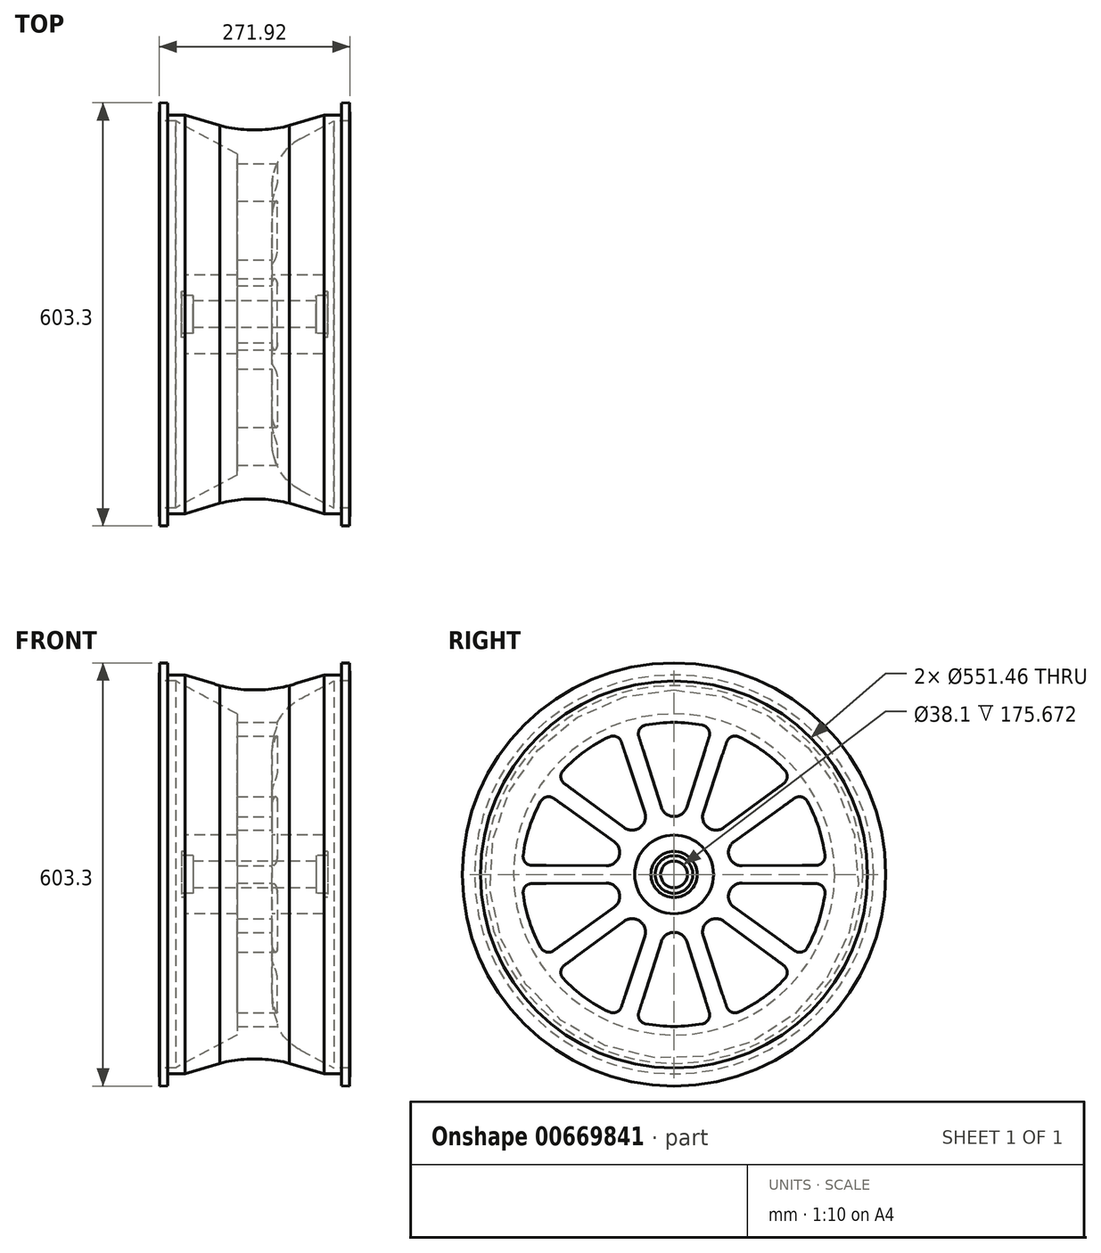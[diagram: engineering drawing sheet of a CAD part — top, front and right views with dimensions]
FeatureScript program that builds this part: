
annotation { "Feature Type Name" : "Feature", "Feature Type Description" : "" }
export const myFeature = defineFeature(function(context is Context, id is Id, definition is map)
    precondition{}
    {
        {
            var Q0;
            Q0=qCreatedBy(makeId("Front.planeOp"),FACE);
            var sketch = newSketch(context, id + "F0", { "sketchPlane" : qUnion([Q0])});
            skLineSegment(sketch, "E0", {"start": v(24.77, 228.87) * mm, "end": v(112.73, 275.73) * mm});
            skLineSegment(sketch, "E1", {"start": v(112.73, 275.73) * mm, "end": v(135.96, 275.73) * mm});
            skLineSegment(sketch, "E2", {"start": v(135.96, 275.73) * mm, "end": v(135.22, 301.65) * mm});
            skLineSegment(sketch, "E3", {"start": v(135.22, 301.65) * mm, "end": v(124.06, 301.33) * mm});
            skLineSegment(sketch, "E4", {"start": v(124.06, 301.33) * mm, "end": v(124.55, 284.39) * mm});
            skLineSegment(sketch, "E5", {"start": v(124.55, 284.39) * mm, "end": v(98.9, 284.39) * mm});
            skLineSegment(sketch, "E6", {"start": v(98.9, 284.39) * mm, "end": v(49.45, 269.2) * mm});
            skLineSegment(sketch, "E7", {"start": v(24.77, 228.87) * mm, "end": v(24.77, 56.11) * mm});
            skLineSegment(sketch, "E8", {"start": v(24.77, 56.11) * mm, "end": v(98.35, 56.11) * mm});
            skLineSegment(sketch, "E9", {"start": v(98.35, 56.11) * mm, "end": v(98.35, 32.88) * mm});
            skLineSegment(sketch, "E10", {"start": v(98.35, 32.88) * mm, "end": v(104.43, 32.88) * mm});
            skLineSegment(sketch, "E11", {"start": v(104.43, 32.88) * mm, "end": v(104.43, 26.8) * mm});
            skLineSegment(sketch, "E12", {"start": v(104.43, 26.8) * mm, "end": v(87.84, 26.8) * mm});
            skLineSegment(sketch, "E13", {"start": v(87.84, 26.8) * mm, "end": v(87.84, 19.05) * mm});
            skLineSegment(sketch, "E14", {"start": v(87.84, 19.05) * mm, "end": v(0, 19.05) * mm});
            skLineSegment(sketch, "E15.MirrorCS", {"start": v(-98.9, 284.39) * mm, "end": v(-49.45, 269.2) * mm});
            skLineSegment(sketch, "E16.MirrorCS", {"start": v(-124.55, 284.39) * mm, "end": v(-98.9, 284.39) * mm});
            skLineSegment(sketch, "E17.MirrorCS", {"start": v(-124.06, 301.33) * mm, "end": v(-124.55, 284.39) * mm});
            skLineSegment(sketch, "E18.MirrorCS", {"start": v(-104.43, 32.88) * mm, "end": v(-104.43, 26.8) * mm});
            skLineSegment(sketch, "E19.MirrorCS", {"start": v(-135.22, 301.65) * mm, "end": v(-124.06, 301.33) * mm});
            skLineSegment(sketch, "E20.MirrorCS", {"start": v(-98.35, 32.88) * mm, "end": v(-104.43, 32.88) * mm});
            skLineSegment(sketch, "E21.MirrorCS", {"start": v(-104.43, 26.8) * mm, "end": v(-87.84, 26.8) * mm});
            skLineSegment(sketch, "E22.MirrorCS", {"start": v(-87.84, 26.8) * mm, "end": v(-87.84, 19.05) * mm});
            skLineSegment(sketch, "E23.MirrorCS", {"start": v(-87.84, 19.05) * mm, "end": v(0, 19.05) * mm});
            skLineSegment(sketch, "E24.MirrorCS", {"start": v(-98.35, 56.11) * mm, "end": v(-98.35, 32.88) * mm});
            skLineSegment(sketch, "E25.MirrorCS", {"start": v(-112.73, 275.73) * mm, "end": v(-135.96, 275.73) * mm});
            skLineSegment(sketch, "E26.MirrorCS", {"start": v(-24.77, 228.87) * mm, "end": v(-112.73, 275.73) * mm});
            skLineSegment(sketch, "E27.MirrorCS", {"start": v(-135.96, 275.73) * mm, "end": v(-135.22, 301.65) * mm});
            skLineSegment(sketch, "E28.MirrorCS", {"start": v(-24.77, 56.11) * mm, "end": v(-98.35, 56.11) * mm});
            skLineSegment(sketch, "E29.MirrorCS", {"start": v(-24.77, 228.87) * mm, "end": v(-24.77, 56.11) * mm});
            skLineSegment(sketch, "E30", {"start": v(-56.5, 0) * mm, "end": v(51.37, 0) * mm});
            skArc(sketch, "E31", {"start": v(-49.45, 269.2) * mm, "mid": v(0, 262.95) * mm, "end": v(49.45, 269.2) * mm});
            skPoint(sketch, "E32.orphan", {"position": v(0, 254) * mm});
            skSolve(sketch);
        }
        {
            var Q0;
            Q0=makeQuery(id+"F0.imprint","IMPRINT",FACE,{"disambiguationData":[TD([[makeQuery(id+"F0.imprint","IMPRINT",EDGE,{"derivedFrom":sQuery(id+"F0.wireOp",EDGE,"E18.MirrorCS")}),1.0]])]});
            var Q1;
            Q1=sQuery(id+"F0.wireOp",EDGE,"E30");
            revolve(context, id + "F1", {"entities" : qUnion([Q0]), "axis" : qUnion([Q1]), "revolveType" : RevolveType.FULL});
        }
        {
            var Q0;
            Q0=makeQuery(id+"F1.opRevolve","SWEPT_FACE",FACE,{"disambiguationData":[OSD([sQuery(id+"F0.wireOp",EDGE,"E7")])]});
            var sketch = newSketch(context, id + "F2", { "sketchPlane" : qUnion([Q0])});
            skCircle(sketch, "E33", {"center": v(0, 0) * mm, "radius": 63.5 * mm});
            skCircle(sketch, "E34", {"center": v(0, 0) * mm, "radius": 69.85 * mm});
            skCircle(sketch, "E35", {"center": v(0, 0) * mm, "radius": 228.6 * mm});
            skCircle(sketch, "E36", {"center": v(0, 0) * mm, "radius": 222.25 * mm});
            skArc(sketch, "E37", {"start": v(50.2, 196.6) * mm, "mid": v(49, 206.95) * mm, "end": v(40.47, 212.92) * mm});
            skArc(sketch, "E38", {"start": v(-40.47, 212.92) * mm, "mid": v(-49, 206.95) * mm, "end": v(-50.2, 196.6) * mm});
            skArc(sketch, "E39", {"start": v(-18.15, 95.83) * mm, "mid": v(0, 82.55) * mm, "end": v(18.15, 95.83) * mm});
            skLineSegment(sketch, "E40", {"start": v(-50.2, 196.6) * mm, "end": v(-18.15, 95.83) * mm});
            skLineSegment(sketch, "E41", {"start": v(18.15, 95.83) * mm, "end": v(50.2, 196.6) * mm});
            skArc(sketch, "E42", {"start": v(40.47, 212.92) * mm, "mid": v(0, 216.73) * mm, "end": v(-40.47, 212.92) * mm});
            skArc(sketch, "E43.1.0", {"start": v(-74.94, 188.56) * mm, "mid": v(-82, 196.23) * mm, "end": v(-92.4, 196.04) * mm});
            skLineSegment(sketch, "E43.1.1", {"start": v(-156.17, 129.54) * mm, "end": v(-71.01, 66.85) * mm});
            skArc(sketch, "E43.1.2", {"start": v(-92.4, 196.04) * mm, "mid": v(-127.4, 175.34) * mm, "end": v(-157.9, 148.47) * mm});
            skLineSegment(sketch, "E43.1.3", {"start": v(-41.64, 88.2) * mm, "end": v(-74.94, 188.56) * mm});
            skArc(sketch, "E43.1.4", {"start": v(-71.01, 66.85) * mm, "mid": v(-48.52, 66.78) * mm, "end": v(-41.64, 88.2) * mm});
            skArc(sketch, "E43.1.5", {"start": v(-157.9, 148.47) * mm, "mid": v(-161.29, 138.62) * mm, "end": v(-156.17, 129.54) * mm});
            skArc(sketch, "E43.2.0", {"start": v(-171.46, 108.5) * mm, "mid": v(-181.67, 110.56) * mm, "end": v(-190, 104.29) * mm});
            skLineSegment(sketch, "E43.2.1", {"start": v(-202.49, 13) * mm, "end": v(-96.75, 12.35) * mm});
            skArc(sketch, "E43.2.2", {"start": v(-190, 104.29) * mm, "mid": v(-206.12, 66.97) * mm, "end": v(-215, 27.3) * mm});
            skLineSegment(sketch, "E43.2.3", {"start": v(-85.53, 46.88) * mm, "end": v(-171.46, 108.5) * mm});
            skArc(sketch, "E43.2.4", {"start": v(-96.75, 12.35) * mm, "mid": v(-78.5, 25.5) * mm, "end": v(-85.53, 46.88) * mm});
            skArc(sketch, "E43.2.5", {"start": v(-215, 27.3) * mm, "mid": v(-211.96, 17.34) * mm, "end": v(-202.49, 13) * mm});
            skArc(sketch, "E43.3.0", {"start": v(-202.49, -13) * mm, "mid": v(-211.96, -17.34) * mm, "end": v(-215, -27.3) * mm});
            skLineSegment(sketch, "E43.3.1", {"start": v(-171.46, -108.5) * mm, "end": v(-85.53, -46.88) * mm});
            skArc(sketch, "E43.3.2", {"start": v(-215, -27.3) * mm, "mid": v(-206.12, -66.97) * mm, "end": v(-190, -104.29) * mm});
            skLineSegment(sketch, "E43.3.3", {"start": v(-96.75, -12.35) * mm, "end": v(-202.49, -13) * mm});
            skArc(sketch, "E43.3.4", {"start": v(-85.53, -46.88) * mm, "mid": v(-78.5, -25.5) * mm, "end": v(-96.75, -12.35) * mm});
            skArc(sketch, "E43.3.5", {"start": v(-190, -104.29) * mm, "mid": v(-181.67, -110.56) * mm, "end": v(-171.46, -108.5) * mm});
            skArc(sketch, "E43.4.0", {"start": v(-156.17, -129.54) * mm, "mid": v(-161.29, -138.62) * mm, "end": v(-157.9, -148.47) * mm});
            skLineSegment(sketch, "E43.4.1", {"start": v(-74.94, -188.56) * mm, "end": v(-41.64, -88.2) * mm});
            skArc(sketch, "E43.4.2", {"start": v(-157.9, -148.47) * mm, "mid": v(-127.4, -175.34) * mm, "end": v(-92.4, -196.04) * mm});
            skLineSegment(sketch, "E43.4.3", {"start": v(-71.01, -66.85) * mm, "end": v(-156.17, -129.54) * mm});
            skArc(sketch, "E43.4.4", {"start": v(-41.64, -88.2) * mm, "mid": v(-48.52, -66.78) * mm, "end": v(-71.01, -66.85) * mm});
            skArc(sketch, "E43.4.5", {"start": v(-92.4, -196.04) * mm, "mid": v(-82, -196.23) * mm, "end": v(-74.94, -188.56) * mm});
            skArc(sketch, "E43.5.0", {"start": v(-50.2, -196.6) * mm, "mid": v(-49, -206.95) * mm, "end": v(-40.47, -212.92) * mm});
            skLineSegment(sketch, "E43.5.1", {"start": v(50.2, -196.6) * mm, "end": v(18.15, -95.83) * mm});
            skArc(sketch, "E43.5.2", {"start": v(-40.47, -212.92) * mm, "mid": v(0, -216.73) * mm, "end": v(40.47, -212.92) * mm});
            skLineSegment(sketch, "E43.5.3", {"start": v(-18.15, -95.83) * mm, "end": v(-50.2, -196.6) * mm});
            skArc(sketch, "E43.5.4", {"start": v(18.15, -95.83) * mm, "mid": v(0, -82.55) * mm, "end": v(-18.15, -95.83) * mm});
            skArc(sketch, "E43.5.5", {"start": v(40.47, -212.92) * mm, "mid": v(49, -206.95) * mm, "end": v(50.2, -196.6) * mm});
            skArc(sketch, "E43.6.0", {"start": v(74.94, -188.56) * mm, "mid": v(82, -196.23) * mm, "end": v(92.4, -196.04) * mm});
            skLineSegment(sketch, "E43.6.1", {"start": v(156.17, -129.54) * mm, "end": v(71.01, -66.85) * mm});
            skArc(sketch, "E43.6.2", {"start": v(92.4, -196.04) * mm, "mid": v(127.4, -175.34) * mm, "end": v(157.9, -148.47) * mm});
            skLineSegment(sketch, "E43.6.3", {"start": v(41.64, -88.2) * mm, "end": v(74.94, -188.56) * mm});
            skArc(sketch, "E43.6.4", {"start": v(71.01, -66.85) * mm, "mid": v(48.52, -66.78) * mm, "end": v(41.64, -88.2) * mm});
            skArc(sketch, "E43.6.5", {"start": v(157.9, -148.47) * mm, "mid": v(161.29, -138.62) * mm, "end": v(156.17, -129.54) * mm});
            skArc(sketch, "E43.7.0", {"start": v(171.46, -108.5) * mm, "mid": v(181.67, -110.56) * mm, "end": v(190, -104.29) * mm});
            skLineSegment(sketch, "E43.7.1", {"start": v(202.49, -13) * mm, "end": v(96.75, -12.35) * mm});
            skArc(sketch, "E43.7.2", {"start": v(190, -104.29) * mm, "mid": v(206.12, -66.97) * mm, "end": v(215, -27.3) * mm});
            skLineSegment(sketch, "E43.7.3", {"start": v(85.53, -46.88) * mm, "end": v(171.46, -108.5) * mm});
            skArc(sketch, "E43.7.4", {"start": v(96.75, -12.35) * mm, "mid": v(78.5, -25.5) * mm, "end": v(85.53, -46.88) * mm});
            skArc(sketch, "E43.7.5", {"start": v(215, -27.3) * mm, "mid": v(211.96, -17.34) * mm, "end": v(202.49, -13) * mm});
            skArc(sketch, "E43.8.0", {"start": v(202.49, 13) * mm, "mid": v(211.96, 17.34) * mm, "end": v(215, 27.3) * mm});
            skLineSegment(sketch, "E43.8.1", {"start": v(171.46, 108.5) * mm, "end": v(85.53, 46.88) * mm});
            skArc(sketch, "E43.8.2", {"start": v(215, 27.3) * mm, "mid": v(206.12, 66.97) * mm, "end": v(190, 104.29) * mm});
            skLineSegment(sketch, "E43.8.3", {"start": v(96.75, 12.35) * mm, "end": v(202.49, 13) * mm});
            skArc(sketch, "E43.8.4", {"start": v(85.53, 46.88) * mm, "mid": v(78.5, 25.5) * mm, "end": v(96.75, 12.35) * mm});
            skArc(sketch, "E43.8.5", {"start": v(190, 104.29) * mm, "mid": v(181.67, 110.56) * mm, "end": v(171.46, 108.5) * mm});
            skArc(sketch, "E43.9.0", {"start": v(156.17, 129.54) * mm, "mid": v(161.29, 138.62) * mm, "end": v(157.9, 148.47) * mm});
            skLineSegment(sketch, "E43.9.1", {"start": v(74.94, 188.56) * mm, "end": v(41.64, 88.2) * mm});
            skArc(sketch, "E43.9.2", {"start": v(157.9, 148.47) * mm, "mid": v(127.4, 175.34) * mm, "end": v(92.4, 196.04) * mm});
            skLineSegment(sketch, "E43.9.3", {"start": v(71.01, 66.85) * mm, "end": v(156.17, 129.54) * mm});
            skArc(sketch, "E43.9.4", {"start": v(41.64, 88.2) * mm, "mid": v(48.52, 66.78) * mm, "end": v(71.01, 66.85) * mm});
            skArc(sketch, "E43.9.5", {"start": v(92.4, 196.04) * mm, "mid": v(82, 196.23) * mm, "end": v(74.94, 188.56) * mm});
            skSolve(sketch);
        }
        {
            var Q0;
            {var subQ0=sQuery(id+"F2.wireOp",EDGE,"E43.2.4");Q0=makeQuery(id+"F2.imprint","IMPRINT",FACE,{"disambiguationData":[TD([[makeQuery(id+"F2.imprint","IMPRINT",EDGE,{"derivedFrom":subQ0}),1.0]])]});}
            var Q1;
            {var subQ0=sQuery(id+"F2.wireOp",EDGE,"E43.3.4");Q1=makeQuery(id+"F2.imprint","IMPRINT",FACE,{"disambiguationData":[TD([[makeQuery(id+"F2.imprint","IMPRINT",EDGE,{"derivedFrom":subQ0}),1.0]])]});}
            var Q2;
            {var subQ0=sQuery(id+"F2.wireOp",EDGE,"E43.4.4");Q2=makeQuery(id+"F2.imprint","IMPRINT",FACE,{"disambiguationData":[TD([[makeQuery(id+"F2.imprint","IMPRINT",EDGE,{"derivedFrom":subQ0}),1.0]])]});}
            var Q3;
            {var subQ0=sQuery(id+"F2.wireOp",EDGE,"E43.5.4");Q3=makeQuery(id+"F2.imprint","IMPRINT",FACE,{"disambiguationData":[TD([[makeQuery(id+"F2.imprint","IMPRINT",EDGE,{"derivedFrom":subQ0}),1.0]])]});}
            var Q4;
            {var subQ0=sQuery(id+"F2.wireOp",EDGE,"E43.6.4");Q4=makeQuery(id+"F2.imprint","IMPRINT",FACE,{"disambiguationData":[TD([[makeQuery(id+"F2.imprint","IMPRINT",EDGE,{"derivedFrom":subQ0}),1.0]])]});}
            var Q5;
            {var subQ0=sQuery(id+"F2.wireOp",EDGE,"E43.7.4");Q5=makeQuery(id+"F2.imprint","IMPRINT",FACE,{"disambiguationData":[TD([[makeQuery(id+"F2.imprint","IMPRINT",EDGE,{"derivedFrom":subQ0}),1.0]])]});}
            var Q6;
            {var subQ0=sQuery(id+"F2.wireOp",EDGE,"E43.8.4");Q6=makeQuery(id+"F2.imprint","IMPRINT",FACE,{"disambiguationData":[TD([[makeQuery(id+"F2.imprint","IMPRINT",EDGE,{"derivedFrom":subQ0}),1.0]])]});}
            var Q7;
            {var subQ0=sQuery(id+"F2.wireOp",EDGE,"E43.9.4");Q7=makeQuery(id+"F2.imprint","IMPRINT",FACE,{"disambiguationData":[TD([[makeQuery(id+"F2.imprint","IMPRINT",EDGE,{"derivedFrom":subQ0}),1.0]])]});}
            var Q8;
            {var subQ0=sQuery(id+"F2.wireOp",EDGE,"E39");Q8=makeQuery(id+"F2.imprint","IMPRINT",FACE,{"disambiguationData":[TD([[makeQuery(id+"F2.imprint","IMPRINT",EDGE,{"derivedFrom":subQ0}),1.0]])]});}
            var Q9;
            {var subQ0=sQuery(id+"F2.wireOp",EDGE,"E43.1.4");Q9=makeQuery(id+"F2.imprint","IMPRINT",FACE,{"disambiguationData":[TD([[makeQuery(id+"F2.imprint","IMPRINT",EDGE,{"derivedFrom":subQ0}),1.0]])]});}
            extrude(context, id + "F3", {"entities" : qUnion([Q0, Q1, Q2, Q3, Q4, Q5, Q6, Q7, Q8, Q9]), "operationType" : NewBodyOperationType.REMOVE, "endBound" : BoundingType.THROUGH_ALL, "oppositeDirection" : true, "depth" : 25.4 * mm, "offsetDistance" : 25.4 * mm, "hasSecondDirection" : true, "secondDirectionOppositeDirection" : false, "secondDirectionDepth" : 25.4 * mm});
        }
        {
            var Q0;
            Q0=makeQuery(id+"F1.opRevolve","SWEPT_EDGE",EDGE,{"disambiguationData":[OSD([sQuery(id+"F0.wireOp",EDGE,"E0"),sQuery(id+"F0.wireOp",EDGE,"E7")])]});
            fillet(context, id + "F4", {"entities" : qUnion([Q0]), "radius" : 76.2 * mm, "tangentPropagation" : true, "allowEdgeOverflow" : false});
        }
    });
